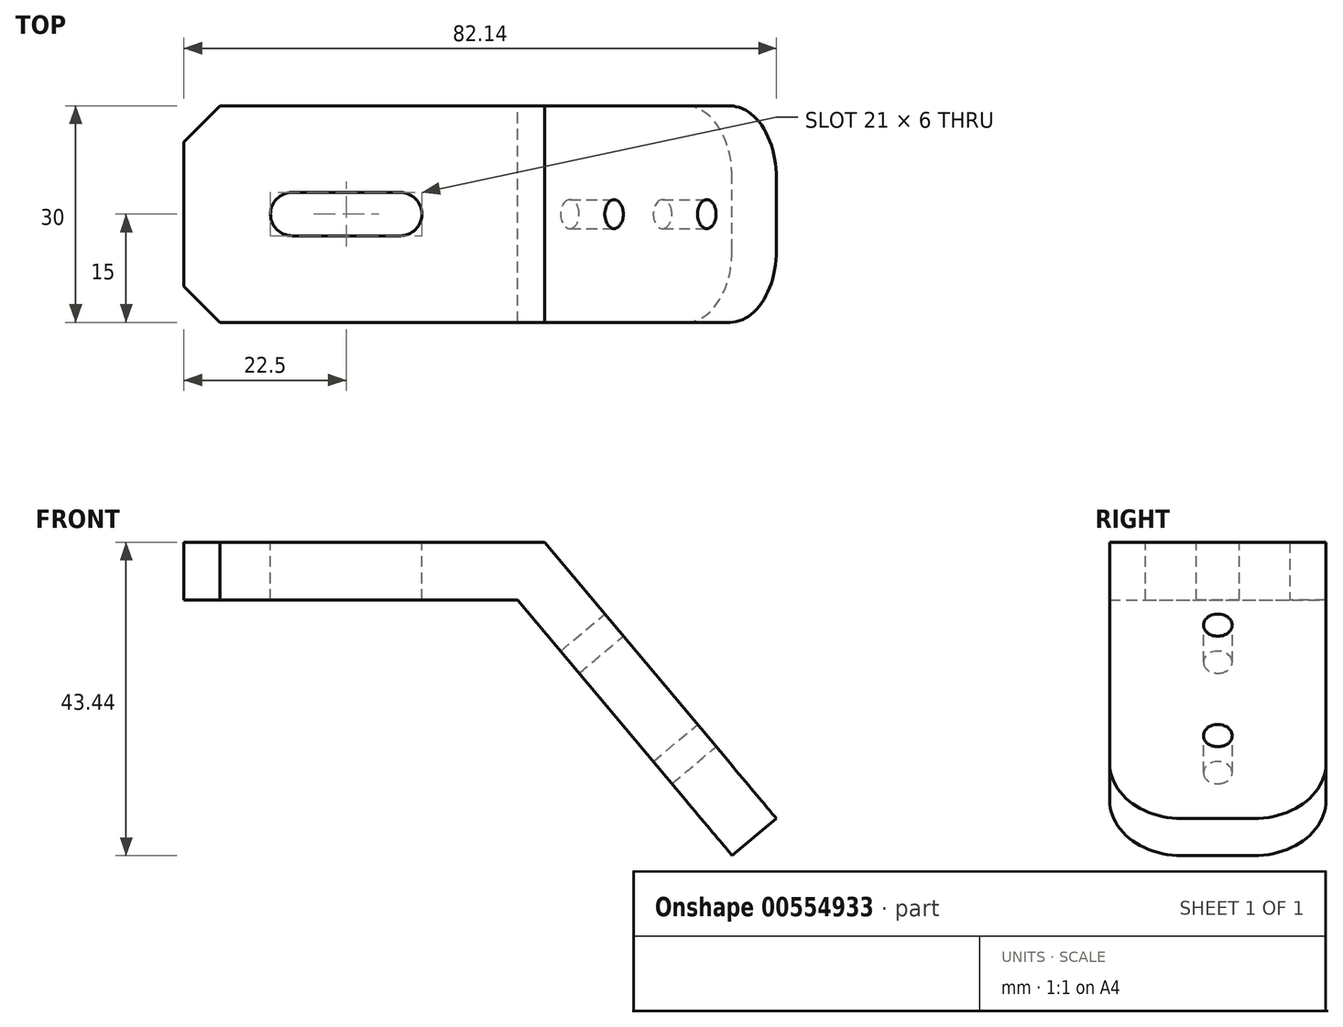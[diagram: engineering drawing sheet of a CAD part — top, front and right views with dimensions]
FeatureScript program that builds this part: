
annotation { "Feature Type Name" : "Feature", "Feature Type Description" : "" }
export const myFeature = defineFeature(function(context is Context, id is Id, definition is map)
    precondition{}
    {
        {
            var Q0;
            Q0=qCreatedBy(makeId("Front.planeOp"),FACE);
            var sketch = newSketch(context, id + "F0", { "sketchPlane" : qUnion([Q0])});
            skLineSegment(sketch, "E0", {"start": v(-50, 0) * mm, "end": v(0, 0) * mm});
            skLineSegment(sketch, "E1", {"start": v(0, 0) * mm, "end": v(32.14, -38.3) * mm});
            skLineSegment(sketch, "E2.0", {"start": v(-3.73, -8) * mm, "end": v(26.01, -43.44) * mm});
            skLineSegment(sketch, "E2.1", {"start": v(-50, -8) * mm, "end": v(-3.73, -8) * mm});
            skLineSegment(sketch, "E3", {"start": v(-50, 0) * mm, "end": v(-50, -8) * mm});
            skLineSegment(sketch, "E4", {"start": v(32.14, -38.3) * mm, "end": v(26.01, -43.44) * mm});
            skSolve(sketch);
        }
        {
            var Q0;
            Q0 = qSketchRegion(id + "F0", true);
            extrude(context, id + "F1", {"entities" : qUnion([Q0]), "endBound" : BoundingType.SYMMETRIC, "depth" : 30 * mm, "offsetDistance" : 25 * mm});
        }
        {
            var Q0;
            Q0=makeQuery(id+"F1.opExtrude","SWEPT_FACE",FACE,{"disambiguationData":[OSD([sQuery(id+"F0.wireOp",EDGE,"E0")])]});
            var sketch = newSketch(context, id + "F2", { "sketchPlane" : qUnion([Q0])});
            skLineSegment(sketch, "E5", {"start": v(-35, 0) * mm, "end": v(-20, 0) * mm});
            skArc(sketch, "E6.0.startCap", {"start": v(-35, -3) * mm, "mid": v(-38, 0) * mm, "end": v(-35, 3) * mm});
            skArc(sketch, "E6.0.endCap", {"start": v(-20, 3) * mm, "mid": v(-17, 0) * mm, "end": v(-20, -3) * mm});
            skLineSegment(sketch, "E6.0.left", {"start": v(-35, 3) * mm, "end": v(-20, 3) * mm});
            skLineSegment(sketch, "E6.0.right", {"start": v(-35, -3) * mm, "end": v(-20, -3) * mm});
            skSolve(sketch);
        }
        {
            var Q0;
            Q0 = qSketchRegion(id + "F2", true);
            extrude(context, id + "F3", {"entities" : qUnion([Q0]), "operationType" : NewBodyOperationType.REMOVE, "endBound" : BoundingType.THROUGH_ALL, "oppositeDirection" : true, "depth" : 25 * mm, "offsetDistance" : 25 * mm});
        }
        {
            var Q0;
            Q0=makeQuery(id+"F1.opExtrude","SWEPT_FACE",FACE,{"disambiguationData":[OSD([sQuery(id+"F0.wireOp",EDGE,"E1")])]});
            var sketch = newSketch(context, id + "F4", { "sketchPlane" : qUnion([Q0])});
            skPoint(sketch, "E7", {"position": v(0, -15) * mm});
            skPoint(sketch, "E8", {"position": v(0, -35) * mm});
            skSolve(sketch);
        }
        {
            var Q0;
            Q0=sQuery(id+"F4.wireOp",VERTEX,"E7");
            var Q1;
            Q1=sQuery(id+"F4.wireOp",VERTEX,"E8");
            var Q2;
            Q2=makeQuery(id+"F1.opExtrude","SWEPT_BODY",BODY,{"disambiguationData":[OSD([sQuery(id+"F0.wireOp",EDGE,"E0"),sQuery(id+"F0.wireOp",EDGE,"E1"),sQuery(id+"F0.wireOp",EDGE,"E2.0"),sQuery(id+"F0.wireOp",EDGE,"E2.1"),sQuery(id+"F0.wireOp",EDGE,"E3"),sQuery(id+"F0.wireOp",EDGE,"E4")])]});
            hole(context, id + "F5", {"style" : HoleStyle.SIMPLE, "endStyle" : HoleEndStyle.THROUGH, "holeDiameter" : 4 * mm, "isTappedThrough" : true, "tappedDepth" : 12 * mm, "tapClearance" : 3, "locations" : qUnion([Q0, Q1]), "scope" : qUnion([Q2])});
        }
        {
            var Q0;
            Q0=makeQuery(id+"F1.opExtrude","CAP_EDGE",EDGE,{"disambiguationData":[OSD([sQuery(id+"F0.wireOp",EDGE,"E4")])],"isStart":true});
            var Q1;
            Q1=makeQuery(id+"F1.opExtrude","CAP_EDGE",EDGE,{"disambiguationData":[OSD([sQuery(id+"F0.wireOp",EDGE,"E4")])],"isStart":false});
            fillet(context, id + "F6", {"entities" : qUnion([Q0, Q1]), "radius" : 10 * mm, "tangentPropagation" : true, "allowEdgeOverflow" : false});
        }
        {
            var Q0;
            Q0=makeQuery(id+"F1.opExtrude","CAP_EDGE",EDGE,{"disambiguationData":[OSD([sQuery(id+"F0.wireOp",EDGE,"E3")])],"isStart":false});
            var Q1;
            Q1=makeQuery(id+"F1.opExtrude","CAP_EDGE",EDGE,{"disambiguationData":[OSD([sQuery(id+"F0.wireOp",EDGE,"E3")])],"isStart":true});
            chamfer(context, id + "F7", {"entities" : qUnion([Q0, Q1]), "width" : 5 * mm, "tangentPropagation" : true});
        }
    });
